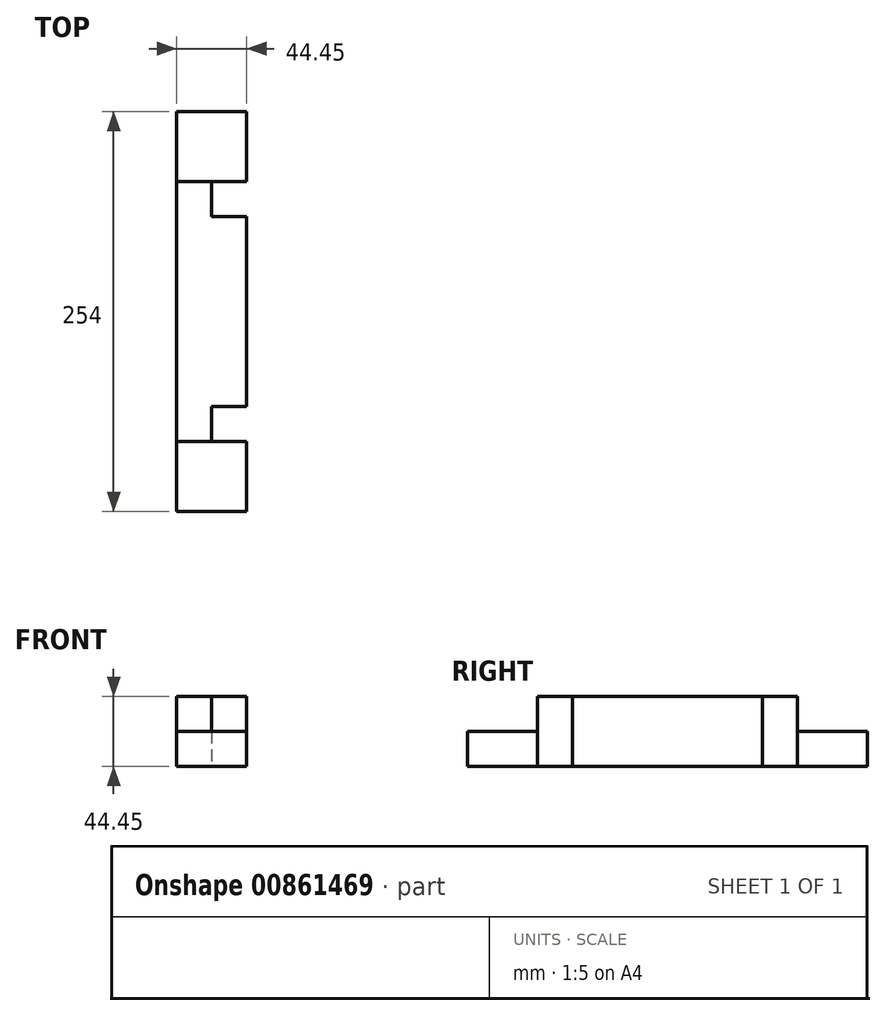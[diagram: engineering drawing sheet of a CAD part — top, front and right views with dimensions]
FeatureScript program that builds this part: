
annotation { "Feature Type Name" : "Feature", "Feature Type Description" : "" }
export const myFeature = defineFeature(function(context is Context, id is Id, definition is map)
    precondition{}
    {
        {
            var Q0;
            Q0=qCreatedBy(makeId("Front.planeOp"),FACE);
            var sketch = newSketch(context, id + "F0", { "sketchPlane" : qUnion([Q0])});
            skLineSegment(sketch, "E0.bottom", {"start": v(0, 0) * mm, "end": v(44.45, 0) * mm});
            skLineSegment(sketch, "E0.top", {"start": v(0, 44.45) * mm, "end": v(44.45, 44.45) * mm});
            skLineSegment(sketch, "E0.left", {"start": v(0, 0) * mm, "end": v(0, 44.45) * mm});
            skLineSegment(sketch, "E0.right", {"start": v(44.45, 0) * mm, "end": v(44.45, 44.45) * mm});
            skSolve(sketch);
        }
        {
            var Q0;
            Q0=makeQuery(id+"F0.imprint","IMPRINT",FACE,{"disambiguationData":[TD([[makeQuery(id+"F0.imprint","IMPRINT",EDGE,{"derivedFrom":sQuery(id+"F0.wireOp",EDGE,"E0.bottom")}),1.0]])]});
            extrude(context, id + "F1", {"entities" : qUnion([Q0]), "depth" : 254 * mm, "offsetDistance" : 25.4 * mm});
        }
        {
            var Q0;
            Q0=makeQuery(id+"F1.opExtrude","SWEPT_FACE",FACE,{"disambiguationData":[OSD([sQuery(id+"F0.wireOp",EDGE,"E0.top")])]});
            var sketch = newSketch(context, id + "F2", { "sketchPlane" : qUnion([Q0])});
            skLineSegment(sketch, "E1.bottom", {"start": v(0, -254) * mm, "end": v(44.45, -254) * mm});
            skLineSegment(sketch, "E1.top", {"start": v(0, -209.55) * mm, "end": v(44.45, -209.55) * mm});
            skLineSegment(sketch, "E1.left", {"start": v(0, -254) * mm, "end": v(0, -209.55) * mm});
            skLineSegment(sketch, "E1.right", {"start": v(44.45, -254) * mm, "end": v(44.45, -209.55) * mm});
            skLineSegment(sketch, "E2.bottom", {"start": v(0, 0) * mm, "end": v(44.45, 0) * mm});
            skLineSegment(sketch, "E2.top", {"start": v(0, -44.45) * mm, "end": v(44.45, -44.45) * mm});
            skLineSegment(sketch, "E2.left", {"start": v(0, 0) * mm, "end": v(0, -44.45) * mm});
            skLineSegment(sketch, "E2.right", {"start": v(44.45, 0) * mm, "end": v(44.45, -44.45) * mm});
            skSolve(sketch);
        }
        {
            var Q0;
            Q0=qSketchRegion(id+"F2",true);
            extrude(context, id + "F3", {"entities" : qUnion([Q0]), "operationType" : NewBodyOperationType.REMOVE, "oppositeDirection" : true, "depth" : 22.22 * mm, "offsetDistance" : 25.4 * mm});
        }
        {
            var Q0;
            Q0=makeQuery(id+"F1.opExtrude","SWEPT_FACE",FACE,{"disambiguationData":[OSD([sQuery(id+"F0.wireOp",EDGE,"E0.right")])]});
            var sketch = newSketch(context, id + "F4", { "sketchPlane" : qUnion([Q0])});
            skLineSegment(sketch, "E3.bottom", {"start": v(-209.55, 44.45) * mm, "end": v(-187.33, 44.45) * mm});
            skLineSegment(sketch, "E3.top", {"start": v(-209.55, 0) * mm, "end": v(-187.33, 0) * mm});
            skLineSegment(sketch, "E3.left", {"start": v(-209.55, 44.45) * mm, "end": v(-209.55, 0) * mm});
            skLineSegment(sketch, "E3.right", {"start": v(-187.33, 44.45) * mm, "end": v(-187.33, 0) * mm});
            skLineSegment(sketch, "E4.bottom", {"start": v(-44.45, 44.45) * mm, "end": v(-66.67, 44.45) * mm});
            skLineSegment(sketch, "E4.top", {"start": v(-44.45, 0) * mm, "end": v(-66.67, 0) * mm});
            skLineSegment(sketch, "E4.left", {"start": v(-44.45, 44.45) * mm, "end": v(-44.45, 0) * mm});
            skLineSegment(sketch, "E4.right", {"start": v(-66.67, 44.45) * mm, "end": v(-66.67, 0) * mm});
            skSolve(sketch);
        }
        {
            var Q0;
            Q0 = qSketchRegion(id + "F4", true);
            extrude(context, id + "F5", {"entities" : qUnion([Q0]), "operationType" : NewBodyOperationType.REMOVE, "oppositeDirection" : true, "depth" : 22.22 * mm, "offsetDistance" : 25.4 * mm});
        }
    });
